# Revit family: Medical_All_Hill-Rom_Connex-Vital-Signs-Monitor
name_source: partatom
category: Specialty Equipment
revit_build: Autodesk Revit Architecture 2015 (Build: 20140606_1530(x64)
units: mm (PartAtom-declared; Revit-internal decimal feet)

## types (1)
- Connex Vital Signs Monitor 6700/6800
    Ambient Temperature = 50 – 104°F (10 – 40°C)
    Apparent Load = 0 VA
    BIMobject category = All
    BIMobject category code = medical-all
    BIMobject main category = Medical
    BIMobject main category code = medical
    Basic Material = Plastic-Hill-Rom-White
    Battery Recharge Time = 4 hours
    Brand url = https://construction.hill-rom.com
    CO2_INPT_Connector_Descr = CO2 sampling input connector
    CO2_OUT_Connector_Descr = CO2 sampling exhaust port
    Depth = 0' - 6 1/32"
    Description = Intuitive, touchscreen monitor for improved workflows and training
    Design country = United States
    Directions for Use = http://www.welchallyn.com
    Edition number = 1
    Ethernet_Connector_Descr = Ethernet RJ-45
    Frequency = 60 Hz
    Full Load Current = 2 A
    Height = 0' - 10"
    Installation instructions = https://construction.hill-rom.com
    Logo Material_Blue = Plastic-Hill-Rom-Light Blue_logo
    Logo Material_Green = Plastic-Hill-Rom-Light Green_logo
    Manufacturer = WelchAllyn
    Manufacturer country = United States
    Manufacturer name = Hill-Rom
    Masterformat 2014 Code = 11 70 00
    Masterformat 2014 Description = Healthcare Equipment
    Model = Connex Vital Signs Monitor 6700/6800
    NBS Reference Code = 75-50
    NBS Reference Description = Medical Safety Systems
    Nominal height = 0' - 0"
    Nominal width = 0' - 0"
    OmniClass Code = 23-25 00 00
    OmniClass Description = Medical and Laboratory Equipment
    Operating Time = 47 patient exams per charge (A patient exam includes NIBP, temperature and SpO₂ measurements at the rate of one patient every 10 minutes with a two-minute display time-out setting and a new battery.)
    Power Factor = 1
    Power_Connector_Descr = Power Connection
    Product Brochure - Doctor's Office = http://www.welchallyn.com
    Product Brochure - Hospital = http://www.welchallyn.com
    Product Guid = 88cad41c-c67b-4ab7-b821-9fa1980a1316
    Product Part Numbers = http://www.welchallyn.com
    Product SKU = WelchAllyn-ConnexVitalSignsMonitor
    Product Specifications = http://www.welchallyn.com
    Product data url = https://bimobject.com
    Product family = Vital Signs Monitoring
    Product group = CVSM
    Product url = https://www.welchallyn.com
    QR code = http://bimobject.com
    Relative Humidity = 15% to 90%
    Set-Up Guide = http://www.welchallyn.com
    Technical description = https://construction.hill-rom.com
    URL = www.welchallyn.com
    USB_Connector_Descr = USB External Connection
    Uniclass 1.4 Code = L852
    Uniclass 1.4 Description = Medical furniture, fittings
    Uniclass 2.0 Code = SS-75-50
    Uniclass 2.0 Description = Medical Safety Systems
    Uniclass 2015 Code = Pr_40_70_51
    Uniclass 2015 Name = Medical and laboratory equipment
    Voltage = 15 V
    Weight = 9.50 lb
    Width = 0' - 11 3/8"
    Youtube clip = https://www.youtube.com

## geometry (parser evidence)
native form markers: Blend x10, Sweep x2
no freeform markers — native parametric forms only
